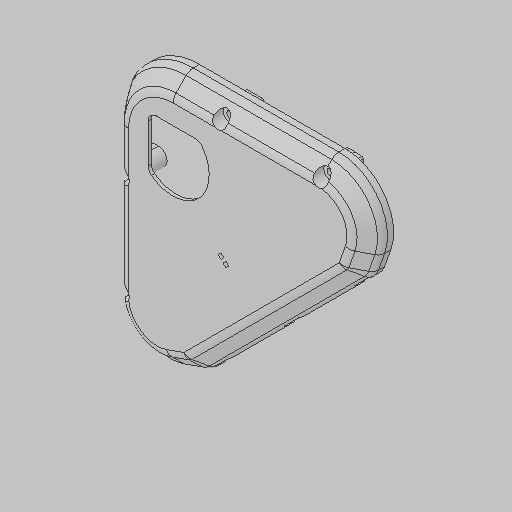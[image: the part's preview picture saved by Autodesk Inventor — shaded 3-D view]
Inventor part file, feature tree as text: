
AUTODESK INVENTOR PART (.ipt)
format: ipt  version: 2023.5 (Build 275446000, 446)  size: 577,536 bytes
history: native  units: in
note: dims shown in document units (in); Inventor stores cm internally (conversion verified against a paired STEP export)
features: extrude x1, hole x1, fillet x1
ambient origin geometry x8: Origin, YZ Plane, XZ Plane, XY Plane, X Axis, Y Axis, Z Axis, Center Point
bodies: Solid2 (feature_tree), Solid1 (feature_tree)
feature tree (3):
  extrude  "Extrusion1"  Depth=0.27in
  hole  "Hole1"  [1 undecoded]
  fillet  "Fillet1"  Radius=0.025in
note: 1 required parameter value undecoded (feature->parameter linkage not recoverable at this tier; creation-order binding heuristic only, values carry confidence <= 0.55)
